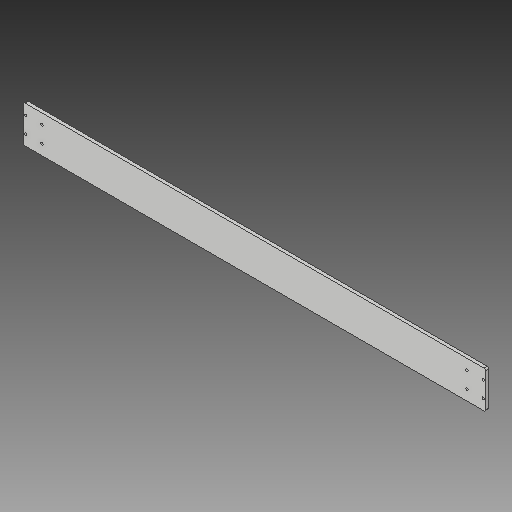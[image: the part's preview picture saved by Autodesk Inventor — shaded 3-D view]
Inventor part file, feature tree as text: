
AUTODESK INVENTOR PART (.ipt)
format: ipt  version: 2019 (Build 230136000, 136)  size: 128,512 bytes
history: native  units: in
note: dims shown in document units (in); Inventor stores cm internally (conversion verified against a paired STEP export)
features: reference x6, other x3, extrude x1, fillet x1, sketch x1, helix x1
ambient origin geometry x8: Origin, YZ Plane, XZ Plane, XY Plane, X Axis, Y Axis, Z Axis, Center Point
bodies: Solid1 (feature_tree)
feature tree (13):
  extrude  "Extrusion1"  Depth=0.0787in
  fillet  "Fillet1"  Radius=0.1181in
  sketch  "Sketch1"  dims[d0=0.1181in d1=0.1181in d2=0.1181in d3=0.1181in d4=0.1181in d5=0.1181in d6=0.1181in d7=0.1181in d8=0.1575in d9=0.0in d10=0.0787in]
  reference  "Reference1"
  reference  "Reference2"
  reference  "Reference3"
  reference  "Reference4"
  reference  "Reference5"
  reference  "Reference6"
  other  "<userpath>\Documents\CAD Files\Helix DLP\Helix DLP.iam"
  helix  "Helix DLP.iam"  [1 undecoded]
  other  "MGN12H, LINEAR GUIDE BLOCK:2"
  other  "MGN12H, LINEAR GUIDE BLOCK:1"
note: 1 required parameter value undecoded (feature->parameter linkage not recoverable at this tier; creation-order binding heuristic only, values carry confidence <= 0.55)
